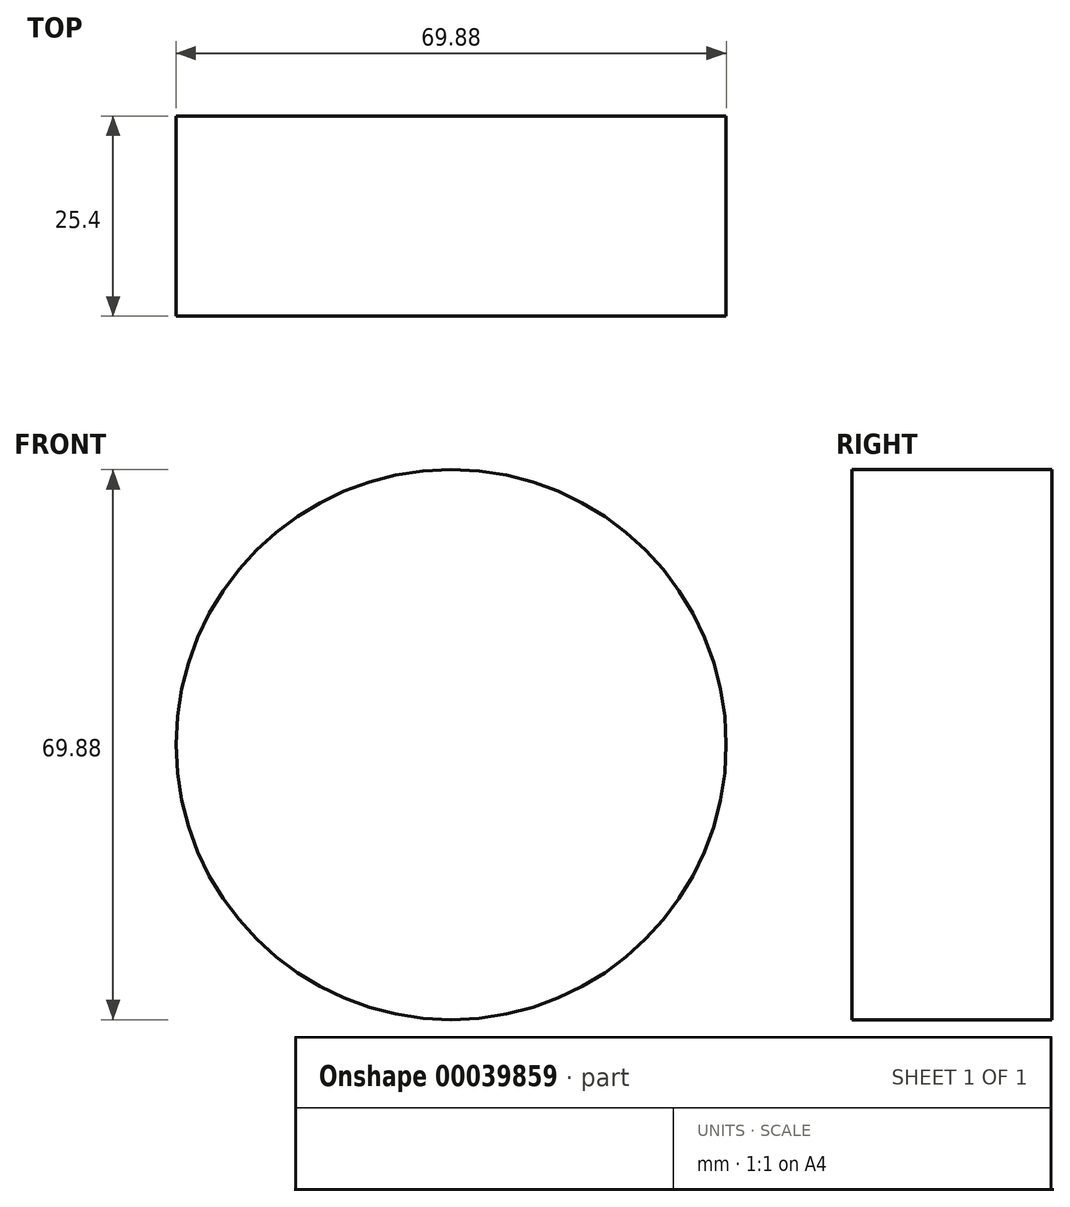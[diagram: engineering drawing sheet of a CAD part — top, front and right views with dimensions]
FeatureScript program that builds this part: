
annotation { "Feature Type Name" : "Feature", "Feature Type Description" : "" }
export const myFeature = defineFeature(function(context is Context, id is Id, definition is map)
    precondition{}
    {
        {
            var Q0;
            Q0=qCreatedBy(makeId("Front.planeOp"),FACE);
            var sketch = newSketch(context, id + "F0", { "sketchPlane" : qUnion([Q0])});
            skCircle(sketch, "E0", {"center": v(0, 0) * mm, "radius": 34.94 * mm});
            skSolve(sketch);
        }
        {
            var Q0;
            Q0=makeQuery(id+"F0.imprint","IMPRINT",FACE,{"disambiguationData":[TD([[makeQuery(id+"F0.imprint","IMPRINT",EDGE,{"derivedFrom":sQuery(id+"F0.wireOp",EDGE,"E0")}),1.0]])]});
            extrude(context, id + "F1", {"entities" : qUnion([Q0]), "depth" : 25.4 * mm});
        }
    });
